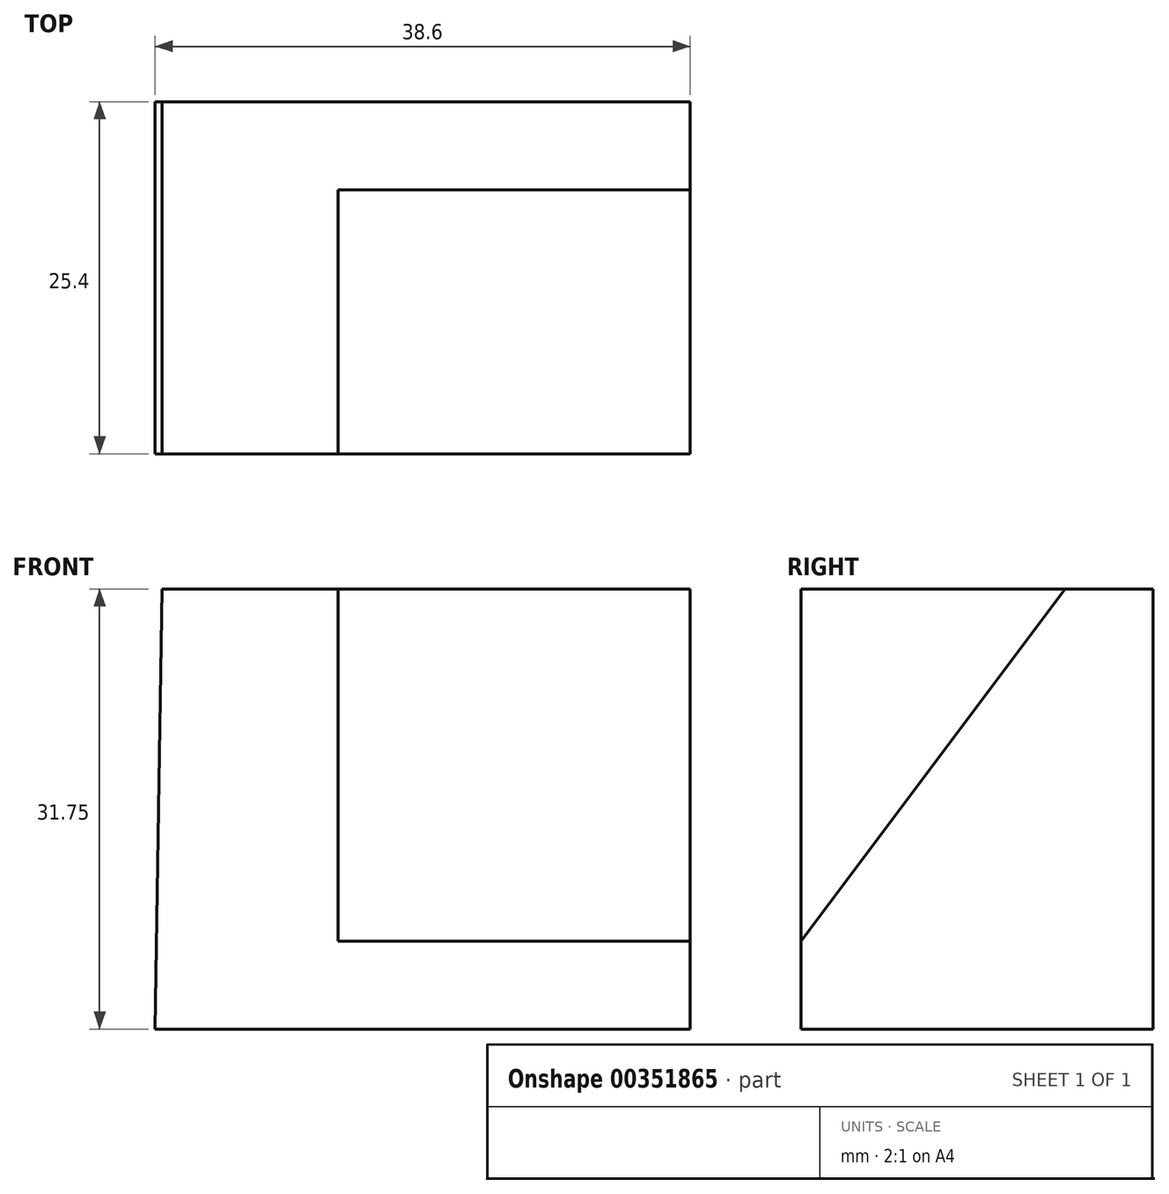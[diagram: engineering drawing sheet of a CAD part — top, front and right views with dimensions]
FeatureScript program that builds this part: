
annotation { "Feature Type Name" : "Feature", "Feature Type Description" : "" }
export const myFeature = defineFeature(function(context is Context, id is Id, definition is map)
    precondition{}
    {
        {
            var Q0;
            Q0=qCreatedBy(makeId("Front.planeOp"),FACE);
            var sketch = newSketch(context, id + "F0", { "sketchPlane" : qUnion([Q0])});
            skLineSegment(sketch, "E0", {"start": v(-48.44, 38.98) * mm, "end": v(-10.34, 38.98) * mm});
            skLineSegment(sketch, "E1", {"start": v(-10.34, 38.98) * mm, "end": v(-10.34, 7.23) * mm});
            skLineSegment(sketch, "E2", {"start": v(-10.34, 7.23) * mm, "end": v(-48.94, 7.23) * mm});
            skLineSegment(sketch, "E3", {"start": v(-48.94, 7.23) * mm, "end": v(-48.44, 38.98) * mm});
            skSolve(sketch);
        }
        {
            var Q0;
            Q0=makeQuery(id+"F0.imprint","IMPRINT",FACE,{"disambiguationData":[TD([[makeQuery(id+"F0.imprint","IMPRINT",EDGE,{"derivedFrom":sQuery(id+"F0.wireOp",EDGE,"E0")}),-1.0]])]});
            extrude(context, id + "F1", {"entities" : qUnion([Q0]), "depth" : 25.4 * mm});
        }
        {
            var Q0;
            Q0=makeQuery(id+"F1.opExtrude","SWEPT_FACE",FACE,{"disambiguationData":[OSD([sQuery(id+"F0.wireOp",EDGE,"E1")])]});
            var sketch = newSketch(context, id + "F2", { "sketchPlane" : qUnion([Q0])});
            skLineSegment(sketch, "E4", {"start": v(-25.4, 13.58) * mm, "end": v(-6.35, 38.98) * mm});
            skLineSegment(sketch, "E5", {"start": v(-25.4, 13.58) * mm, "end": v(-25.4, 38.98) * mm});
            skLineSegment(sketch, "E6", {"start": v(-25.4, 38.98) * mm, "end": v(-6.35, 38.98) * mm});
            skSolve(sketch);
        }
        {
            var Q0;
            Q0=makeQuery(id+"F2.imprint","IMPRINT",FACE,{"disambiguationData":[TD([[makeQuery(id+"F2.imprint","IMPRINT",EDGE,{"derivedFrom":sQuery(id+"F2.wireOp",EDGE,"E4")}),1.0]])]});
            extrude(context, id + "F3", {"entities" : qUnion([Q0]), "operationType" : NewBodyOperationType.REMOVE, "oppositeDirection" : true, "depth" : 25.4 * mm});
        }
    });
